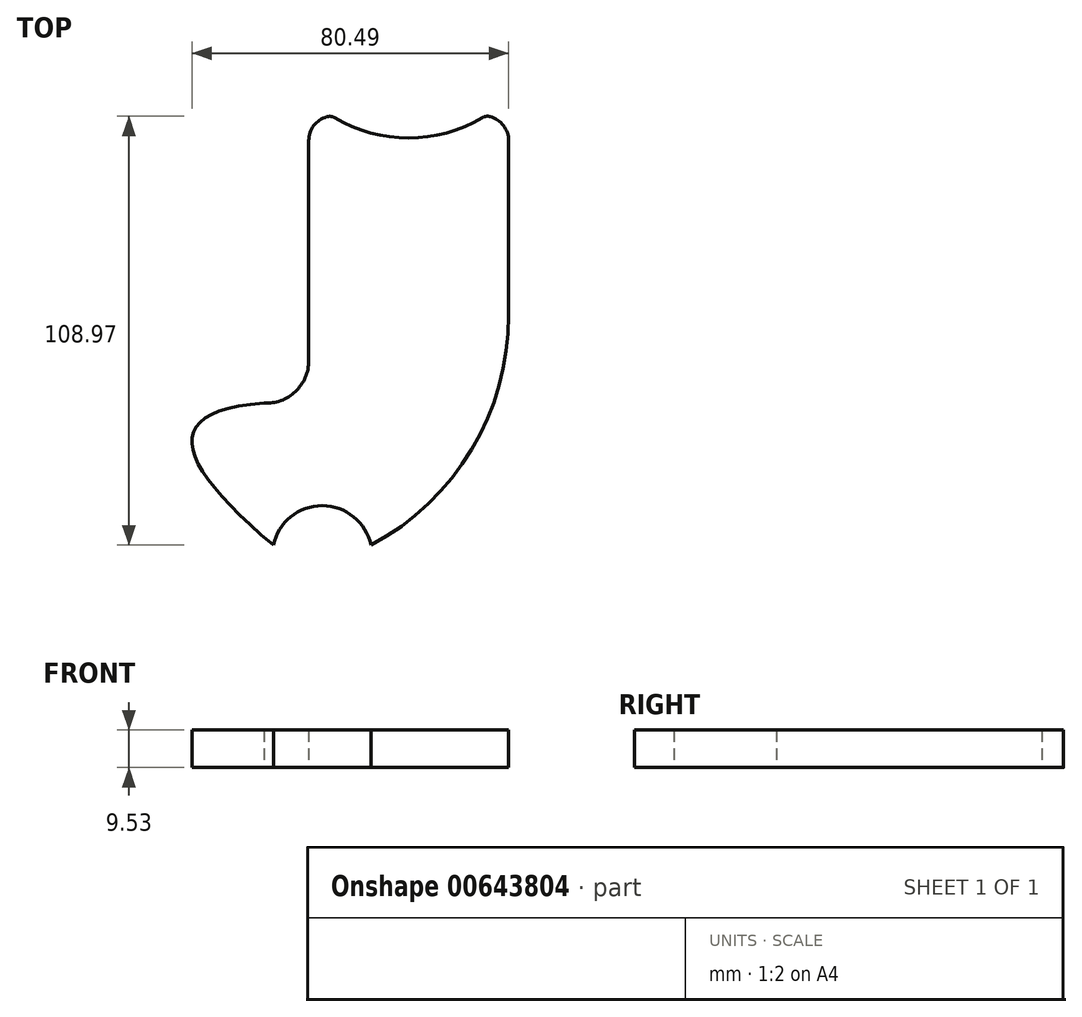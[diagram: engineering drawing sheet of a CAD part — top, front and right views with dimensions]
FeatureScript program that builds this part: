
annotation { "Feature Type Name" : "Feature", "Feature Type Description" : "" }
export const myFeature = defineFeature(function(context is Context, id is Id, definition is map)
    precondition{}
    {
        {
            var Q0;
            Q0=qCreatedBy(makeId("Top.planeOp"),FACE);
            var sketch = newSketch(context, id + "F0", { "sketchPlane" : qUnion([Q0])});
            skLineSegment(sketch, "E0", {"start": v(-4.5, 26.29) * mm, "end": v(-4.5, 82.17) * mm});
            skLineSegment(sketch, "E1", {"start": v(46.3, 82.17) * mm, "end": v(46.3, 54.61) * mm});
            skArc(sketch, "E2", {"start": v(11.34, -20.58) * mm, "mid": v(-1.08, -10.54) * mm, "end": v(-13.5, -20.58) * mm});
            skArc(sketch, "E3", {"start": v(-15.9, 15.5) * mm, "mid": v(-7.88, 18.44) * mm, "end": v(-4.5, 26.29) * mm});
            skFitSpline(sketch, "E4", {"points": [v(-15.9, 15.5) * mm, v(-13.5, -20.58) * mm], "startDerivative": vector(-81.98, -5.77) * mm, "endDerivative": vector(73.14, -61.75) * mm});
            skPoint(sketch, "E5.visualSharp", {"position": v(-4.5, 88.52) * mm});
            skArc(sketch, "E5.filletArc", {"start": v(0.1, 88.27) * mm, "mid": v(-3.23, 85.99) * mm, "end": v(-4.5, 82.17) * mm});
            skPoint(sketch, "E6.visualSharp", {"position": v(46.3, 88.52) * mm});
            skArc(sketch, "E6.filletArc", {"start": v(46.3, 82.17) * mm, "mid": v(44.98, 86.04) * mm, "end": v(41.58, 88.3) * mm});
            skLineSegment(sketch, "E7", {"start": v(46.3, 82.17) * mm, "end": v(46.3, 37.72) * mm});
            skArc(sketch, "E8", {"start": v(11.34, -20.58) * mm, "mid": v(36.89, 3.73) * mm, "end": v(46.3, 37.72) * mm});
            skPoint(sketch, "E9.visualSharp", {"position": v(11.34, -20.58) * mm});
            skArc(sketch, "E10", {"start": v(2.1, 88.01) * mm, "mid": v(20.86, 82.87) * mm, "end": v(39.63, 88.03) * mm});
            skPoint(sketch, "E11.visualSharp", {"position": v(1.3, 88.5) * mm});
            skArc(sketch, "E11.filletArc", {"start": v(2.1, 88.01) * mm, "mid": v(1.12, 88.35) * mm, "end": v(0.1, 88.27) * mm});
            skPoint(sketch, "E12.visualSharp", {"position": v(40.4, 88.5) * mm});
            skArc(sketch, "E12.filletArc", {"start": v(41.58, 88.3) * mm, "mid": v(40.58, 88.36) * mm, "end": v(39.63, 88.03) * mm});
            skLineSegment(sketch, "E13", {"start": v(-4.5, 88.52) * mm, "end": v(72.42, 88.27) * mm, "construction": true});
            skSolve(sketch);
        }
        {
            var Q0;
            Q0=makeQuery(id+"F0.imprint","IMPRINT",FACE,{"disambiguationData":[TD([[makeQuery(id+"F0.imprint","IMPRINT",EDGE,{"derivedFrom":sQuery(id+"F0.wireOp",EDGE,"E0")}),-1.0]])]});
            extrude(context, id + "F1", {"entities" : qUnion([Q0]), "depth" : 9.52 * mm, "offsetDistance" : 25.4 * mm});
        }
    });
